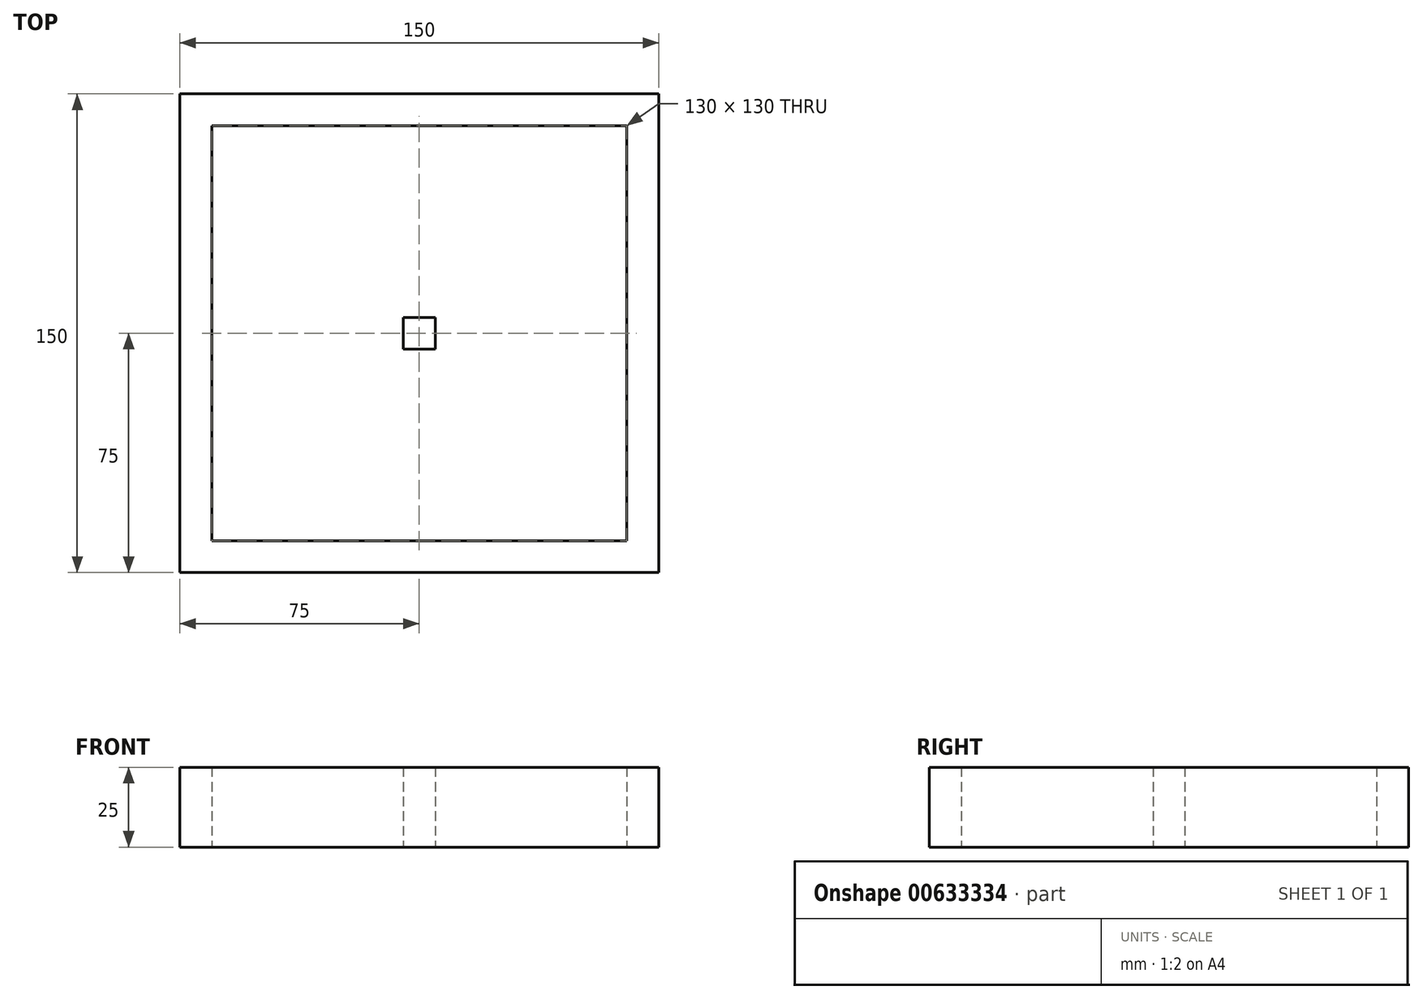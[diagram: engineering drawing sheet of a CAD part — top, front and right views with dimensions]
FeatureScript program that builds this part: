
annotation { "Feature Type Name" : "Feature", "Feature Type Description" : "" }
export const myFeature = defineFeature(function(context is Context, id is Id, definition is map)
    precondition{}
    {
        {
            var Q0;
            Q0=qCreatedBy(makeId("Top.planeOp"),FACE);
            var sketch = newSketch(context, id + "F0", { "sketchPlane" : qUnion([Q0])});
            skLineSegment(sketch, "E0.bottom", {"start": v(75, 75) * mm, "end": v(-75, 75) * mm});
            skLineSegment(sketch, "E0.top", {"start": v(75, -75) * mm, "end": v(-75, -75) * mm});
            skLineSegment(sketch, "E0.left", {"start": v(75, 75) * mm, "end": v(75, -75) * mm});
            skLineSegment(sketch, "E0.right", {"start": v(-75, 75) * mm, "end": v(-75, -75) * mm});
            skPoint(sketch, "E0.middle", {"position": v(0, 0) * mm});
            skLineSegment(sketch, "E1.0", {"start": v(65, 65) * mm, "end": v(-65, 65) * mm});
            skLineSegment(sketch, "E1.1", {"start": v(65, 65) * mm, "end": v(65, -65) * mm});
            skLineSegment(sketch, "E1.2", {"start": v(65, -65) * mm, "end": v(-65, -65) * mm});
            skLineSegment(sketch, "E1.3", {"start": v(-65, 65) * mm, "end": v(-65, -65) * mm});
            skLineSegment(sketch, "E2.bottom", {"start": v(5, 65) * mm, "end": v(-5, 65) * mm});
            skLineSegment(sketch, "E2.top", {"start": v(5, -65) * mm, "end": v(-5, -65) * mm});
            skLineSegment(sketch, "E2.left", {"start": v(5, 65) * mm, "end": v(5, -65) * mm});
            skLineSegment(sketch, "E2.right", {"start": v(-5, 65) * mm, "end": v(-5, -65) * mm});
            skLineSegment(sketch, "E3.bottom", {"start": v(65, -5) * mm, "end": v(-65, -5) * mm});
            skLineSegment(sketch, "E3.top", {"start": v(65, 5) * mm, "end": v(-65, 5) * mm});
            skLineSegment(sketch, "E3.left", {"start": v(65, -5) * mm, "end": v(65, 5) * mm});
            skLineSegment(sketch, "E3.right", {"start": v(-65, -5) * mm, "end": v(-65, 5) * mm});
            skSolve(sketch);
        }
        {
            var Q0;
            Q0=makeQuery(id+"F0.imprint","IMPRINT",FACE,{"disambiguationData":[TD([[makeQuery(id+"F0.imprint","IMPRINT",EDGE,{"derivedFrom":sQuery(id+"F0.wireOp",EDGE,"E0.bottom")}),1.0]])]});
            var Q1;
            {var subQ0=sQuery(id+"F0.wireOp",EDGE,"E2.bottom");Q1=makeQuery(id+"F0.imprint","IMPRINT",FACE,{"disambiguationData":[TD([[makeQuery(id+"F0.imprint","IMPRINT",EDGE,{"derivedFrom":subQ0}),1.0]])]});}
            var Q2;
            {var subQ5=sQuery(id+"F0.wireOp",EDGE,"E3.right");Q2=makeQuery(id+"F0.imprint","IMPRINT",FACE,{"disambiguationData":[TD([[makeQuery(id+"F0.imprint","IMPRINT",EDGE,{"derivedFrom":subQ5}),-1.0]])]});}
            var Q3;
            {var subQ0=sQuery(id+"F0.wireOp",EDGE,"E3.top");var subQ1=sQuery(id+"F0.wireOp",EDGE,"E2.left");var subQ2=makeQuery(id+"F0.imprint","INTERSECT",VERTEX,{"derivedFrom":[subQ1,subQ0]});Q3=makeQuery(id+"F0.imprint","IMPRINT",FACE,{"disambiguationData":[TD([[makeQuery(id+"F0.imprint","IMPRINT",EDGE,{"disambiguationData":[TD([[subQ2,-1.0]])],"derivedFrom":subQ1}),-1.0]])]});}
            var Q4;
            {var subQ5=sQuery(id+"F0.wireOp",EDGE,"E3.left");Q4=makeQuery(id+"F0.imprint","IMPRINT",FACE,{"disambiguationData":[TD([[makeQuery(id+"F0.imprint","IMPRINT",EDGE,{"derivedFrom":subQ5}),1.0]])]});}
            var Q5;
            {var subQ0=sQuery(id+"F0.wireOp",EDGE,"E2.top");Q5=makeQuery(id+"F0.imprint","IMPRINT",FACE,{"disambiguationData":[TD([[makeQuery(id+"F0.imprint","IMPRINT",EDGE,{"derivedFrom":subQ0}),-1.0]])]});}
            extrude(context, id + "F1", {"entities" : qUnion([Q0, Q1, Q2, Q3, Q4, Q5]), "depth" : 25 * mm, "offsetDistance" : 25 * mm});
        }
    });
